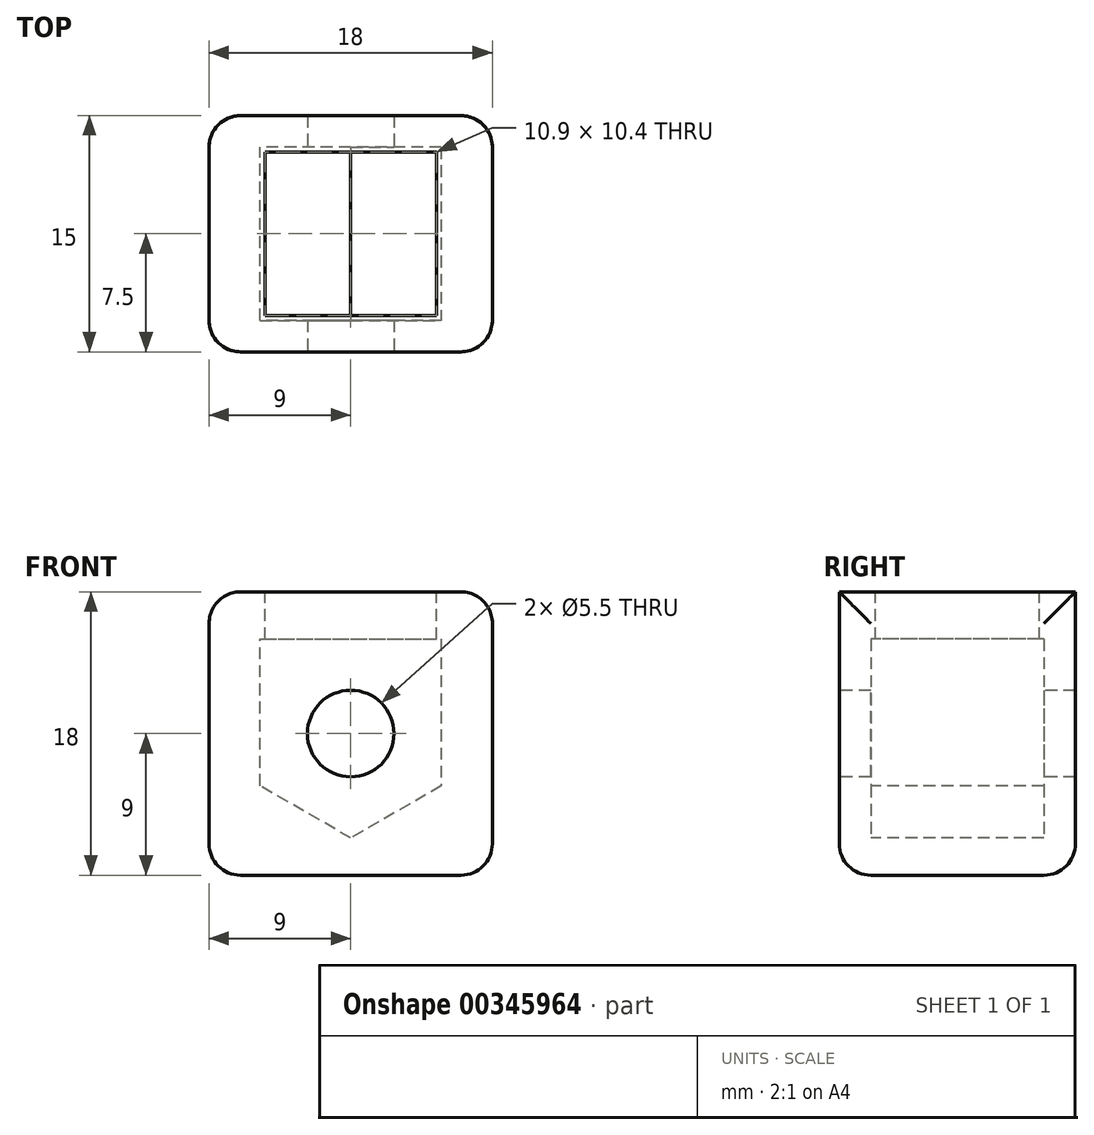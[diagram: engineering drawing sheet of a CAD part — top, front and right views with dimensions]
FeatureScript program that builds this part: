
annotation { "Feature Type Name" : "Feature", "Feature Type Description" : "" }
export const myFeature = defineFeature(function(context is Context, id is Id, definition is map)
    precondition{}
    {
        {
            var Q0;
            Q0=qCreatedBy(makeId("Front.planeOp"),FACE);
            var sketch = newSketch(context, id + "F0", { "sketchPlane" : qUnion([Q0])});
            skLineSegment(sketch, "E0.bottom", {"start": v(-9, 9) * mm, "end": v(9, 9) * mm});
            skLineSegment(sketch, "E0.top", {"start": v(-9, -9) * mm, "end": v(9, -9) * mm});
            skLineSegment(sketch, "E0.left", {"start": v(-9, 9) * mm, "end": v(-9, -9) * mm});
            skLineSegment(sketch, "E0.right", {"start": v(9, 9) * mm, "end": v(9, -9) * mm});
            skLineSegment(sketch, "E1", {"start": v(-9, 9) * mm, "end": v(9, -9) * mm, "construction": true});
            skSolve(sketch);
        }
        {
            var Q0;
            Q0=makeQuery(id+"F0.imprint","IMPRINT",FACE,{"disambiguationData":[TD([[makeQuery(id+"F0.imprint","IMPRINT",EDGE,{"derivedFrom":sQuery(id+"F0.wireOp",EDGE,"E0.bottom")}),-1.0]])]});
            extrude(context, id + "F1", {"entities" : qUnion([Q0]), "depth" : 15 * mm});
        }
        {
            var Q0;
            Q0=makeQuery(id+"F1.opExtrude","CAP_FACE",FACE,{"disambiguationData":[OSD([sQuery(id+"F0.wireOp",EDGE,"E0.bottom"),sQuery(id+"F0.wireOp",EDGE,"E0.top"),sQuery(id+"F0.wireOp",EDGE,"E0.left"),sQuery(id+"F0.wireOp",EDGE,"E0.right")])],"isStart":false});
            cPlane(context, id + "F2", {"entities" : qUnion([Q0]), "cplaneType" : CPlaneType.OFFSET, "offset" : 2 * mm, "oppositeDirection" : true, "width" : 150 * mm, "height" : 150 * mm});
        }
        {
            var Q0;
            Q0=qCreatedBy(id+"F2.planeOp",FACE);
            var sketch = newSketch(context, id + "F3", { "sketchPlane" : qUnion([Q0])});
            skCircle(sketch, "E2.cCircle", {"center": v(0, 0) * mm, "radius": 5.75 * mm, "construction": true});
            skLineSegment(sketch, "E2.0", {"start": v(5.75, 3.32) * mm, "end": v(5.75, -3.32) * mm});
            skLineSegment(sketch, "E2.1", {"start": v(5.75, -3.32) * mm, "end": v(0, -6.64) * mm});
            skLineSegment(sketch, "E2.2", {"start": v(0, -6.64) * mm, "end": v(-5.75, -3.32) * mm});
            skLineSegment(sketch, "E2.3", {"start": v(-5.75, -3.32) * mm, "end": v(-5.75, 3.68) * mm});
            skPoint(sketch, "E2.0.midPoint", {"position": v(5.75, 0) * mm});
            skLineSegment(sketch, "E3.top", {"start": v(-5.75, 9.68) * mm, "end": v(5.75, 9.68) * mm});
            skLineSegment(sketch, "E3.left", {"start": v(-5.75, 3.68) * mm, "end": v(-5.75, 9.68) * mm});
            skLineSegment(sketch, "E3.right", {"start": v(5.75, 3.32) * mm, "end": v(5.75, 9.68) * mm});
            skSolve(sketch);
        }
        {
            var Q0;
            Q0=makeQuery(id+"F1.opExtrude","CAP_FACE",FACE,{"disambiguationData":[OSD([sQuery(id+"F0.wireOp",EDGE,"E0.bottom"),sQuery(id+"F0.wireOp",EDGE,"E0.top"),sQuery(id+"F0.wireOp",EDGE,"E0.left"),sQuery(id+"F0.wireOp",EDGE,"E0.right")])],"isStart":true});
            cPlane(context, id + "F4", {"entities" : qUnion([Q0]), "cplaneType" : CPlaneType.OFFSET, "offset" : 2 * mm, "oppositeDirection" : true, "width" : 150 * mm, "height" : 150 * mm});
        }
        {
            var Q0;
            Q0 = qSketchRegion(id + "F3", true);
            var Q1;
            Q1=qCreatedBy(id+"F4.planeOp",FACE);
            extrude(context, id + "F5", {"entities" : qUnion([Q0]), "operationType" : NewBodyOperationType.REMOVE, "endBound" : BoundingType.UP_TO_SURFACE, "oppositeDirection" : true, "endBoundEntityFace" : qUnion([Q1]), "depth" : 25 * mm});
        }
        {
            var Q0;
            Q0=makeQuery(id+"F1.opExtrude","CAP_FACE",FACE,{"disambiguationData":[OSD([sQuery(id+"F0.wireOp",EDGE,"E0.bottom"),sQuery(id+"F0.wireOp",EDGE,"E0.top"),sQuery(id+"F0.wireOp",EDGE,"E0.left"),sQuery(id+"F0.wireOp",EDGE,"E0.right")])],"isStart":false});
            var sketch = newSketch(context, id + "F6", { "sketchPlane" : qUnion([Q0])});
            skCircle(sketch, "E4", {"center": v(0, 0) * mm, "radius": 2.75 * mm});
            skSolve(sketch);
        }
        {
            var Q0;
            Q0 = qSketchRegion(id + "F6", true);
            extrude(context, id + "F7", {"entities" : qUnion([Q0]), "operationType" : NewBodyOperationType.REMOVE, "endBound" : BoundingType.THROUGH_ALL, "oppositeDirection" : true, "depth" : 25 * mm});
        }
        {
            var Q0;
            Q0=makeQuery(id+"F1.opExtrude","SWEPT_FACE",FACE,{"disambiguationData":[OSD([sQuery(id+"F0.wireOp",EDGE,"E0.left")])]});
            var Q1;
            Q1=makeQuery(id+"F1.opExtrude","SWEPT_FACE",FACE,{"disambiguationData":[OSD([sQuery(id+"F0.wireOp",EDGE,"E0.right")])]});
            var Q2;
            Q2=makeQuery(id+"F1.opExtrude","SWEPT_FACE",FACE,{"disambiguationData":[OSD([sQuery(id+"F0.wireOp",EDGE,"E0.top")])]});
            fillet(context, id + "F8", {"entities" : qUnion([Q0, Q1, Q2]), "radius" : 2 * mm, "tangentPropagation" : true, "allowEdgeOverflow" : false});
        }
        {
            var Q0;
            Q0=makeQuery(id+"F1.opExtrude","SWEPT_FACE",FACE,{"disambiguationData":[OSD([sQuery(id+"F0.wireOp",EDGE,"E0.bottom")])]});
            var sketch = newSketch(context, id + "F9", { "sketchPlane" : qUnion([Q0])});
            skLineSegment(sketch, "E5.bottom", {"start": v(-5.75, -2) * mm, "end": v(5.75, -2) * mm});
            skLineSegment(sketch, "E5.top", {"start": v(-5.75, -13) * mm, "end": v(5.75, -13) * mm});
            skLineSegment(sketch, "E5.left", {"start": v(-5.75, -2) * mm, "end": v(-5.75, -13) * mm});
            skLineSegment(sketch, "E5.right", {"start": v(5.75, -2) * mm, "end": v(5.75, -13) * mm});
            skLineSegment(sketch, "E6.bottom", {"start": v(-5.45, -2.3) * mm, "end": v(5.45, -2.3) * mm});
            skLineSegment(sketch, "E6.top", {"start": v(-5.45, -12.7) * mm, "end": v(5.45, -12.7) * mm});
            skLineSegment(sketch, "E6.left", {"start": v(-5.45, -2.3) * mm, "end": v(-5.45, -12.7) * mm});
            skLineSegment(sketch, "E6.right", {"start": v(5.45, -2.3) * mm, "end": v(5.45, -12.7) * mm});
            skSolve(sketch);
        }
        {
            var Q0;
            Q0 = qSketchRegion(id + "F9", true);
            extrude(context, id + "F10", {"entities" : qUnion([Q0]), "operationType" : NewBodyOperationType.ADD, "oppositeDirection" : true, "depth" : 3 * mm});
        }
    });
